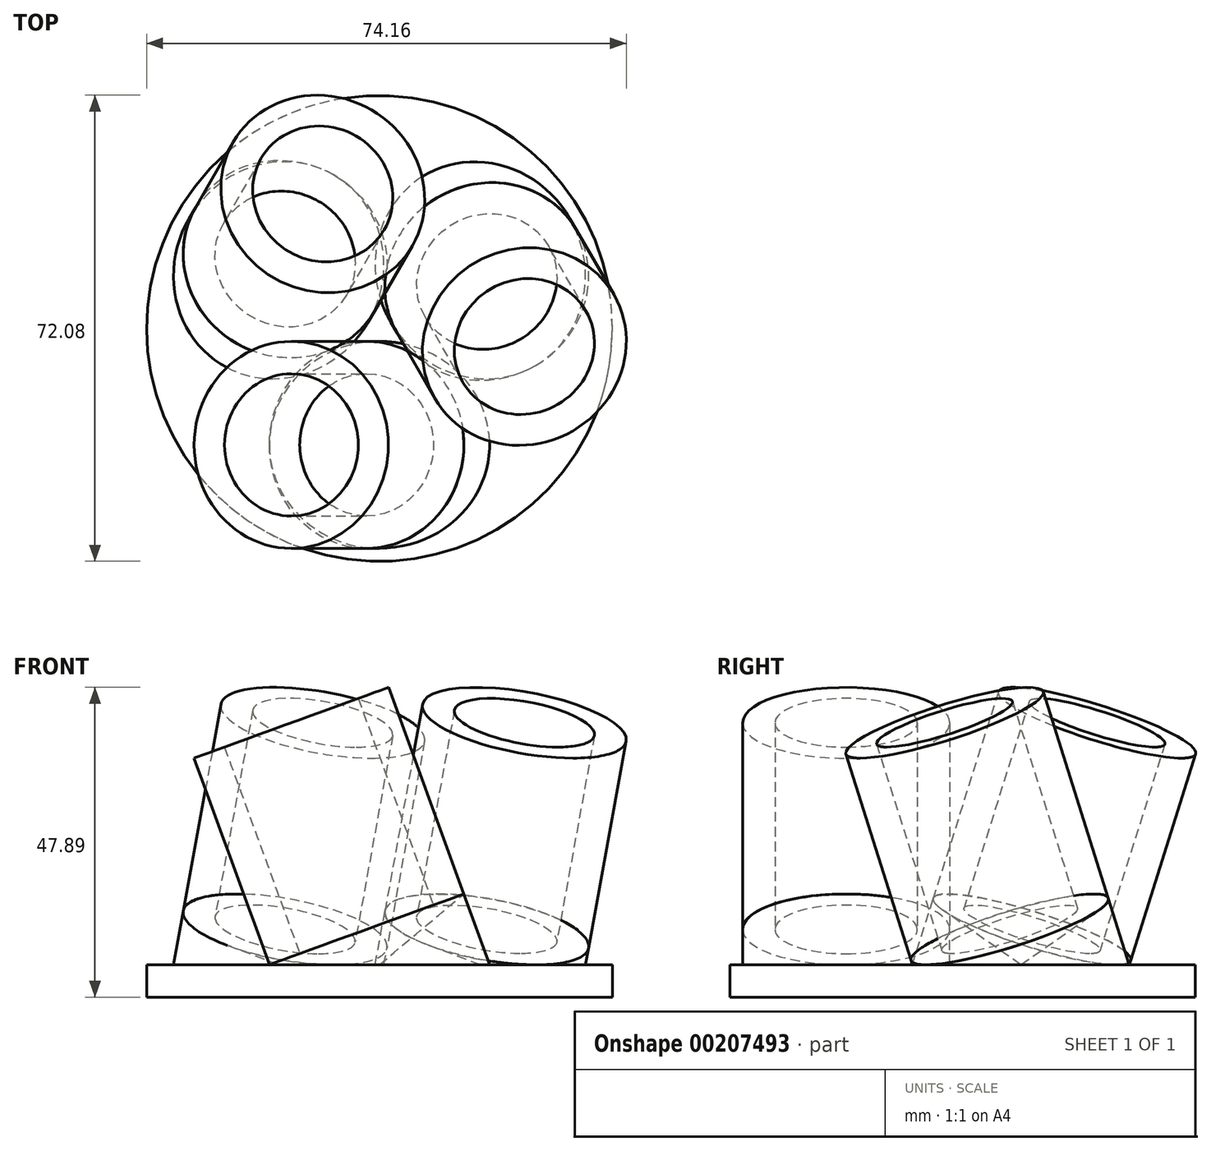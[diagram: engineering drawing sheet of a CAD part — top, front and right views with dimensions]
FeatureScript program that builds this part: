
annotation { "Feature Type Name" : "Feature", "Feature Type Description" : "" }
export const myFeature = defineFeature(function(context is Context, id is Id, definition is map)
    precondition{}
    {
        {
            var Q0;
            Q0=qCreatedBy(makeId("Top.planeOp"),FACE);
            var sketch = newSketch(context, id + "F0", { "sketchPlane" : qUnion([Q0])});
            skCircle(sketch, "E0", {"center": v(0, 0) * mm, "radius": 36 * mm});
            skSolve(sketch);
        }
        {
            var Q0;
            Q0 = qSketchRegion(id + "F0", true);
            extrude(context, id + "F1", {"entities" : qUnion([Q0]), "depth" : 5 * mm});
        }
        {
            var Q0;
            Q0=qCreatedBy(makeId("Front.planeOp"),FACE);
            cPlane(context, id + "F2", {"entities" : qUnion([Q0]), "cplaneType" : CPlaneType.OFFSET, "offset" : 18 * mm, "width" : 150 * mm, "height" : 150 * mm});
        }
        {
            var Q0;
            Q0=qCreatedBy(id+"F2.planeOp",FACE);
            var sketch = newSketch(context, id + "F3", { "sketchPlane" : qUnion([Q0])});
            skLineSegment(sketch, "E1", {"start": v(0, 5) * mm, "end": v(-13.62, 42.42) * mm});
            skLineSegment(sketch, "E2", {"start": v(-13.62, 42.42) * mm, "end": v(-28.66, 36.95) * mm});
            skLineSegment(sketch, "E3", {"start": v(-28.66, 36.95) * mm, "end": v(-17.03, 5) * mm});
            skLineSegment(sketch, "E4", {"start": v(-17.03, 5) * mm, "end": v(0, 5) * mm});
            skLineSegment(sketch, "E5", {"start": v(-17.03, 5) * mm, "end": v(-2, 10.47) * mm});
            skLineSegment(sketch, "E6", {"start": v(-23.96, 38.66) * mm, "end": v(-12.33, 6.71) * mm});
            skLineSegment(sketch, "E7", {"start": v(-2, 10.47) * mm, "end": v(-2, 5) * mm});
            skSolve(sketch);
        }
        {
            var Q0;
            {var subQ0=sQuery(id+"F3.wireOp",EDGE,"E3");Q0=makeQuery(id+"F3.imprint","IMPRINT",FACE,{"disambiguationData":[TD([[makeQuery(id+"F3.imprint","IMPRINT",EDGE,{"derivedFrom":subQ0}),1.0]])]});}
            var Q1;
            {var subQ0=sQuery(id+"F3.wireOp",EDGE,"E4");Q1=makeQuery(id+"F3.imprint","IMPRINT",FACE,{"disambiguationData":[TD([[makeQuery(id+"F3.imprint","IMPRINT",EDGE,{"derivedFrom":subQ0}),1.0]])]});}
            var Q2;
            {var subQ3=sQuery(id+"F3.wireOp",EDGE,"E7");Q2=makeQuery(id+"F3.imprint","IMPRINT",FACE,{"disambiguationData":[TD([[makeQuery(id+"F3.imprint","IMPRINT",EDGE,{"derivedFrom":subQ3}),-1.0]])]});}
            var Q3;
            Q3=sQuery(id+"F3.wireOp",EDGE,"E1");
            revolve(context, id + "F4", {"entities" : qUnion([Q0, Q1, Q2]), "axis" : qUnion([Q3]), "revolveType" : RevolveType.FULL});
        }
        {
            var Q0;
            Q0=makeQuery(id+"F4.opRevolve","SWEPT_FACE",FACE,{"disambiguationData":[OSD([sQuery(id+"F3.wireOp",EDGE,"E5")])]});
            var sketch = newSketch(context, id + "F5", { "sketchPlane" : qUnion([Q0])});
            skCircle(sketch, "E8", {"center": v(1.71, -18) * mm, "radius": 16 * mm});
            skSolve(sketch);
        }
        {
            var Q0;
            Q0 = qSketchRegion(id + "F5", true);
            var Q1;
            Q1=makeQuery(id+"F1.opExtrude","CAP_FACE",FACE,{"disambiguationData":[OSD([sQuery(id+"F0.wireOp",EDGE,"E0")])],"isStart":false});
            extrude(context, id + "F6", {"entities" : qUnion([Q0]), "endBound" : BoundingType.UP_TO_SURFACE, "oppositeDirection" : true, "endBoundEntityFace" : qUnion([Q1]), "depth" : 25 * mm});
        }
        {
            var Q0;
            Q0=makeQuery(id+"F4.opRevolve","SWEPT_BODY",BODY,{"disambiguationData":[OSD([sQuery(id+"F3.wireOp",EDGE,"E1"),sQuery(id+"F3.wireOp",EDGE,"E2"),sQuery(id+"F3.wireOp",EDGE,"E3"),sQuery(id+"F3.wireOp",EDGE,"E4"),sQuery(id+"F3.wireOp",EDGE,"E5"),sQuery(id+"F3.wireOp",EDGE,"E6")])]});
            var Q1;
            Q1=makeQuery(id+"F6.opExtrude","SWEPT_BODY",BODY,{"disambiguationData":[OSD([sQuery(id+"F5.wireOp",EDGE,"E8")])]});
            var Q2;
            Q2=makeQuery(id+"F1.opExtrude","CAP_EDGE",EDGE,{"disambiguationData":[OSD([sQuery(id+"F0.wireOp",EDGE,"E0")])],"isStart":false});
            circularPattern(context, id + "F7", {"entities" : qUnion([Q0, Q1]), "axis" : qUnion([Q2]), "angle" : 360 * degree, "instanceCount" : 3, "equalSpace" : true});
        }
    });
